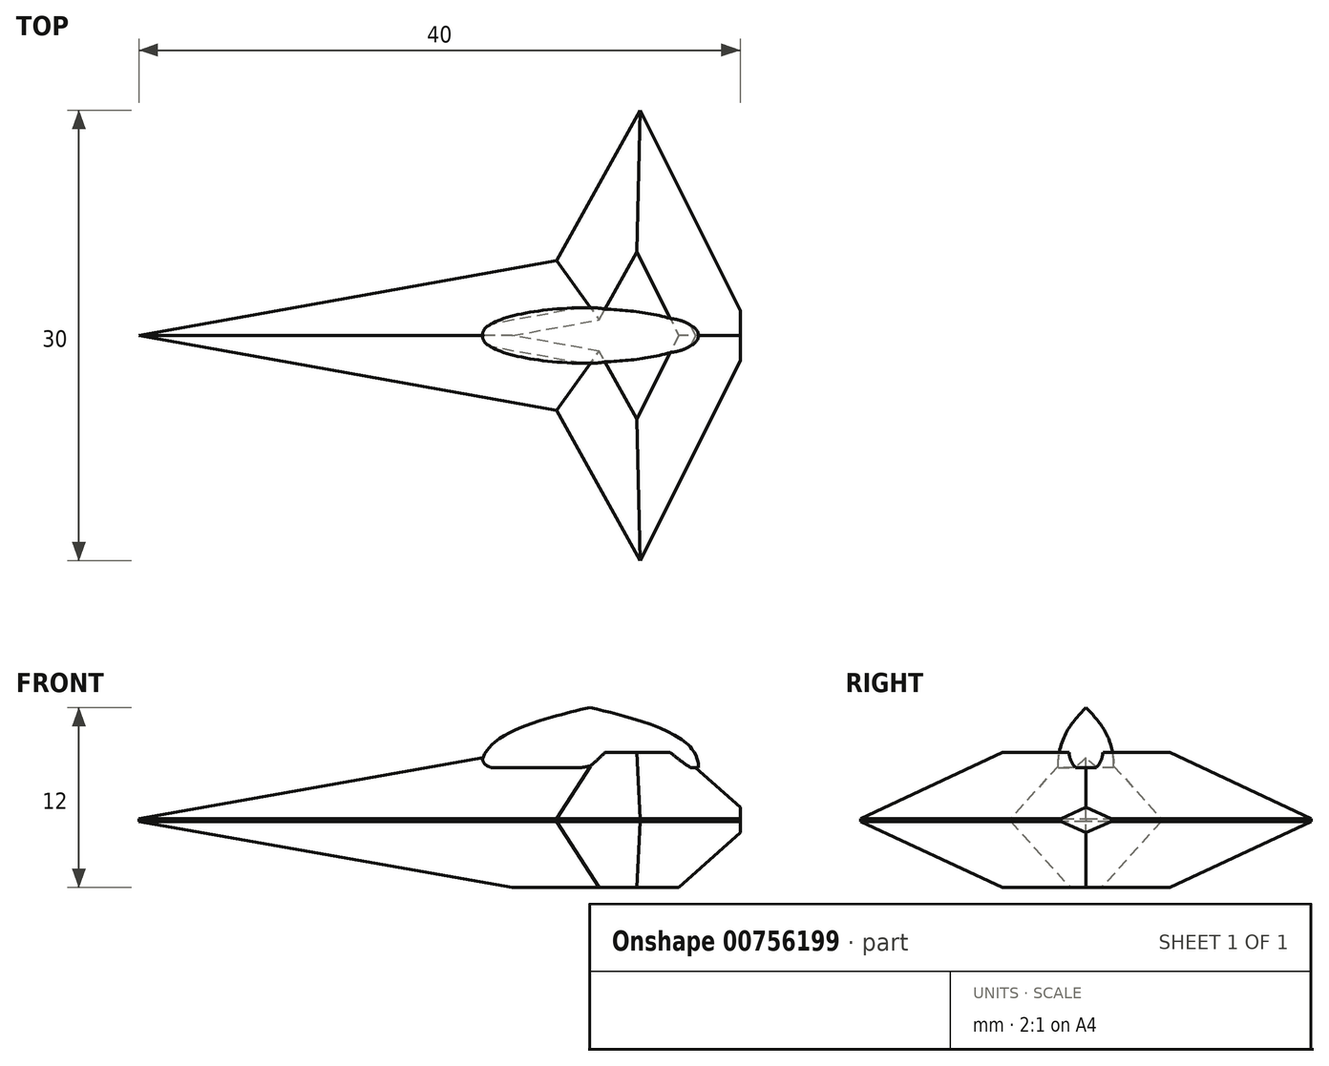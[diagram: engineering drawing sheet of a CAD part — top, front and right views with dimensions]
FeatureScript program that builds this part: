
annotation { "Feature Type Name" : "Feature", "Feature Type Description" : "" }
export const myFeature = defineFeature(function(context is Context, id is Id, definition is map)
    precondition{}
    {
        {
            var Q0;
            Q0=qCreatedBy(makeId("Top.planeOp"),FACE);
            var sketch = newSketch(context, id + "F0", { "sketchPlane" : qUnion([Q0])});
            skLineSegment(sketch, "E0", {"start": v(-27.78, 0) * mm, "end": v(0, 5) * mm});
            skLineSegment(sketch, "E1", {"start": v(0, 5) * mm, "end": v(5.56, 15) * mm});
            skLineSegment(sketch, "E2", {"start": v(5.56, 15) * mm, "end": v(12.22, 1.67) * mm});
            skLineSegment(sketch, "E3.MirrorCS", {"start": v(-27.78, 0) * mm, "end": v(0, -5) * mm});
            skLineSegment(sketch, "E4.MirrorCS", {"start": v(0, -5) * mm, "end": v(5.56, -15) * mm});
            skLineSegment(sketch, "E5.MirrorCS", {"start": v(5.56, -15) * mm, "end": v(12.22, -1.67) * mm});
            skLineSegment(sketch, "E6", {"start": v(12.22, -1.67) * mm, "end": v(12.22, 1.67) * mm});
            skPoint(sketch, "E7.positionSnap0", {"position": v(2.78, 10) * mm});
            skEllipse(sketch, "E8", {"center": v(2.22, 0) * mm, "majorRadius": 7.22 * mm, "minorRadius": 1.85 * mm, "majorAxis": v(-1, 0)});
            skSolve(sketch);
        }
        {
            var Q0;
            Q0=makeQuery(id+"F0.imprint","IMPRINT",FACE,{"disambiguationData":[TD([[makeQuery(id+"F0.imprint","IMPRINT",EDGE,{"derivedFrom":sQuery(id+"F0.wireOp",EDGE,"E0")}),-1.0]])]});
            var Q1;
            Q1=makeQuery(id+"F0.imprint","IMPRINT",FACE,{"disambiguationData":[TD([[makeQuery(id+"F0.imprint","IMPRINT",EDGE,{"derivedFrom":sQuery(id+"F0.wireOp",EDGE,"E8")}),1.0]])]});
            extrude(context, id + "F1", {"entities" : qUnion([Q0, Q1]), "depth" : 9 * mm, "offsetDistance" : 25 * mm, "symmetric" : true});
        }
        {
            var Q0;
            Q0=makeQuery(id+"F1.opExtrude","CAP_EDGE",EDGE,{"disambiguationData":[OSD([sQuery(id+"F0.wireOp",EDGE,"E3.MirrorCS")])],"isStart":false});
            var Q1;
            Q1=makeQuery(id+"F1.opExtrude","CAP_EDGE",EDGE,{"disambiguationData":[OSD([sQuery(id+"F0.wireOp",EDGE,"E0")])],"isStart":false});
            var Q2;
            Q2=makeQuery(id+"F1.opExtrude","CAP_EDGE",EDGE,{"disambiguationData":[OSD([sQuery(id+"F0.wireOp",EDGE,"E1")])],"isStart":false});
            var Q3;
            Q3=makeQuery(id+"F1.opExtrude","CAP_EDGE",EDGE,{"disambiguationData":[OSD([sQuery(id+"F0.wireOp",EDGE,"E1")])],"isStart":true});
            var Q4;
            Q4=makeQuery(id+"F1.opExtrude","CAP_EDGE",EDGE,{"disambiguationData":[OSD([sQuery(id+"F0.wireOp",EDGE,"E4.MirrorCS")])],"isStart":false});
            var Q5;
            Q5=makeQuery(id+"F1.opExtrude","CAP_EDGE",EDGE,{"disambiguationData":[OSD([sQuery(id+"F0.wireOp",EDGE,"E4.MirrorCS")])],"isStart":true});
            var Q6;
            Q6=makeQuery(id+"F1.opExtrude","CAP_EDGE",EDGE,{"disambiguationData":[OSD([sQuery(id+"F0.wireOp",EDGE,"E0")])],"isStart":true});
            var Q7;
            Q7=makeQuery(id+"F1.opExtrude","CAP_EDGE",EDGE,{"disambiguationData":[OSD([sQuery(id+"F0.wireOp",EDGE,"E3.MirrorCS")])],"isStart":true});
            var Q8;
            Q8=makeQuery(id+"F1.opExtrude","CAP_EDGE",EDGE,{"disambiguationData":[OSD([sQuery(id+"F0.wireOp",EDGE,"E2")])],"isStart":true});
            var Q9;
            Q9=makeQuery(id+"F1.opExtrude","CAP_EDGE",EDGE,{"disambiguationData":[OSD([sQuery(id+"F0.wireOp",EDGE,"E5.MirrorCS")])],"isStart":true});
            var Q10;
            Q10=makeQuery(id+"F1.opExtrude","CAP_EDGE",EDGE,{"disambiguationData":[OSD([sQuery(id+"F0.wireOp",EDGE,"E5.MirrorCS")])],"isStart":false});
            var Q11;
            Q11=makeQuery(id+"F1.opExtrude","CAP_EDGE",EDGE,{"disambiguationData":[OSD([sQuery(id+"F0.wireOp",EDGE,"E2")])],"isStart":false});
            chamfer(context, id + "F2", {"entities" : qUnion([Q0, Q1, Q2, Q3, Q4, Q5, Q6, Q7, Q8, Q9, Q10, Q11]), "width" : 4.4 * mm, "tangentPropagation" : true});
        }
        {
            var Q0;
            Q0=qCreatedBy(makeId("Top.planeOp"),FACE);
            cPlane(context, id + "F3", {"entities" : qUnion([Q0]), "cplaneType" : CPlaneType.OFFSET, "offset" : 3.5 * mm, "width" : 150 * mm, "height" : 150 * mm});
        }
        {
            var Q0;
            Q0=qCreatedBy(id+"F3.planeOp",FACE);
            var sketch = newSketch(context, id + "F4", { "sketchPlane" : qUnion([Q0])});
            skEllipse(sketch, "E9", {"center": v(2.22, 0) * mm, "majorRadius": 7.22 * mm, "minorRadius": 1.86 * mm, "majorAxis": v(1, 0)});
            skSolve(sketch);
        }
        {
            var Q0;
            Q0=qCreatedBy(makeId("Top.planeOp"),FACE);
            cPlane(context, id + "F5", {"entities" : qUnion([Q0]), "cplaneType" : CPlaneType.OFFSET, "offset" : 7.5 * mm, "width" : 150 * mm, "height" : 150 * mm});
        }
        {
            var Q0;
            Q0=qCreatedBy(id+"F5.planeOp",FACE);
            var sketch = newSketch(context, id + "F6", { "sketchPlane" : qUnion([Q0])});
            skPoint(sketch, "E10", {"position": v(2.22, 0) * mm});
            skSolve(sketch);
        }
        {
            var Q1;
            Q1 = qSketchRegion(id + "F4", true);
            var Q2;
            Q2=sQuery(id+"F6.wireOp",VERTEX,"E10");
            loft(context, id + "F7", {"operationType" : NewBodyOperationType.ADD, "startCondition" : LoftEndDerivativeType.NORMAL_TO_PROFILE, "startMagnitude" : 1.5, "sheetProfilesArray" : [{ "sheetProfileEntities" : qUnion([Q1]) }, { "sheetProfileEntities" : qUnion([Q2]) }]});
        }
    });
